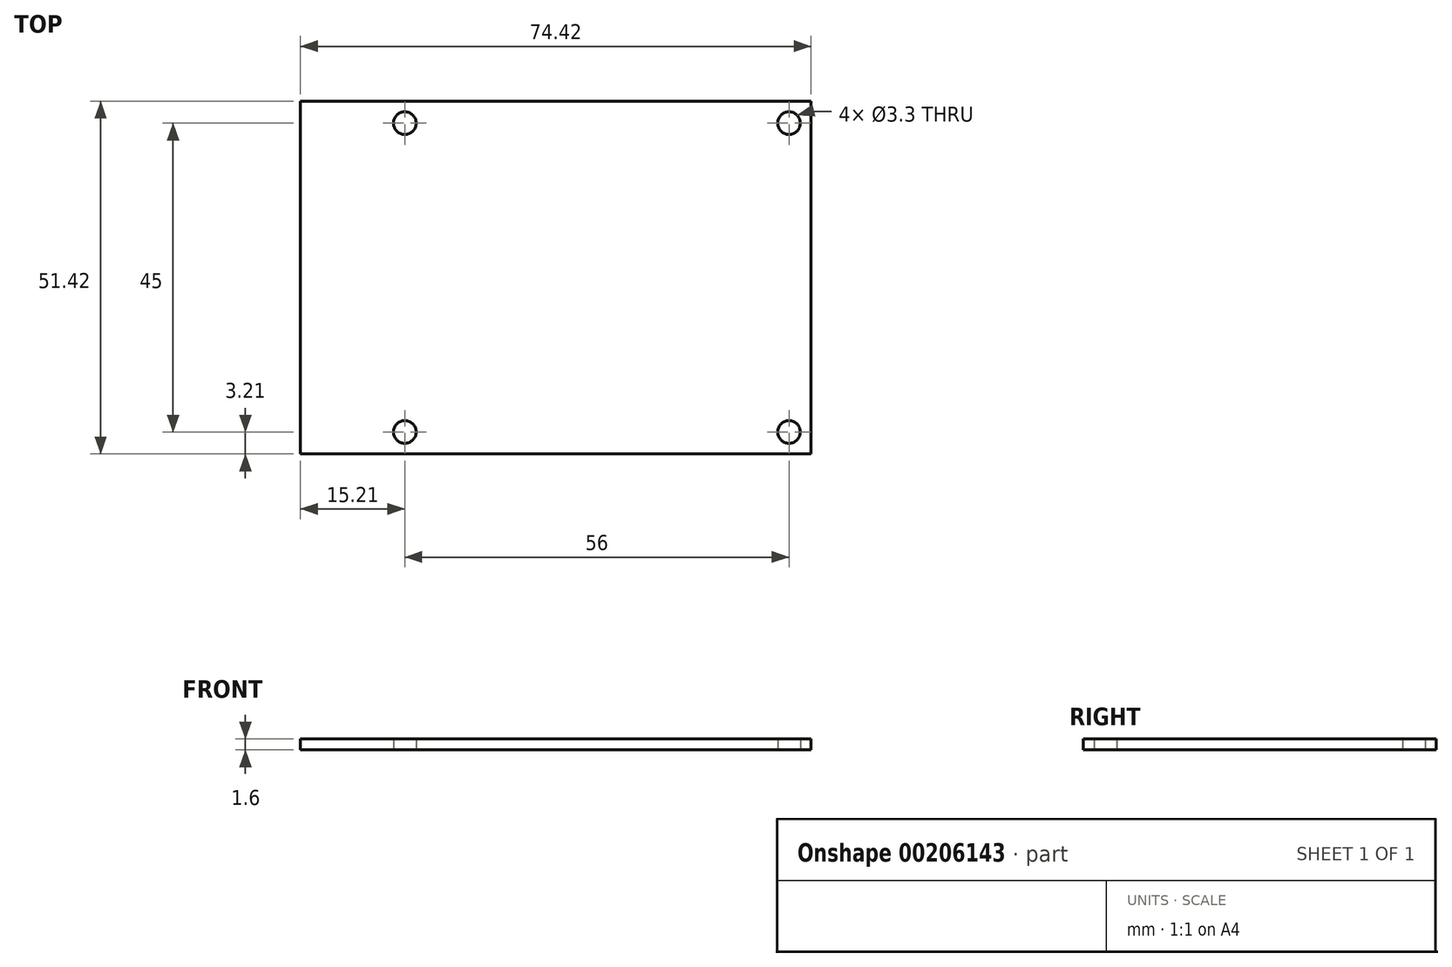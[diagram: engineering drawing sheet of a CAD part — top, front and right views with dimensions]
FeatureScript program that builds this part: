
annotation { "Feature Type Name" : "Feature", "Feature Type Description" : "" }
export const myFeature = defineFeature(function(context is Context, id is Id, definition is map)
    precondition{}
    {
        {
            var Q0;
            Q0=qCreatedBy(makeId("Top.planeOp"),FACE);
            var sketch = newSketch(context, id + "F0", { "sketchPlane" : qUnion([Q0])});
            skLineSegment(sketch, "E0.bottom", {"start": v(37.2, -25.71) * mm, "end": v(-37.21, -25.71) * mm});
            skLineSegment(sketch, "E0.top", {"start": v(37.2, 25.71) * mm, "end": v(-37.21, 25.71) * mm});
            skLineSegment(sketch, "E0.left", {"start": v(37.2, -25.71) * mm, "end": v(37.2, 25.7) * mm});
            skLineSegment(sketch, "E0.right", {"start": v(-37.21, -25.71) * mm, "end": v(-37.21, 25.7) * mm});
            skPoint(sketch, "E0.middle", {"position": v(0, 0) * mm});
            skCircle(sketch, "E1", {"center": v(34, -22.5) * mm, "radius": 1.65 * mm});
            skCircle(sketch, "E2", {"center": v(34, 22.5) * mm, "radius": 1.65 * mm});
            skCircle(sketch, "E3", {"center": v(-22, -22.5) * mm, "radius": 1.65 * mm});
            skCircle(sketch, "E4", {"center": v(-22, 22.5) * mm, "radius": 1.65 * mm});
            skSolve(sketch);
        }
        {
            var Q0;
            Q0=makeQuery(id+"F0.imprint","IMPRINT",FACE,{"disambiguationData":[TD([[makeQuery(id+"F0.imprint","IMPRINT",EDGE,{"derivedFrom":sQuery(id+"F0.wireOp",EDGE,"E0.bottom")}),-1.0]])]});
            extrude(context, id + "F1", {"entities" : qUnion([Q0]), "depth" : 1.6 * mm});
        }
    });
